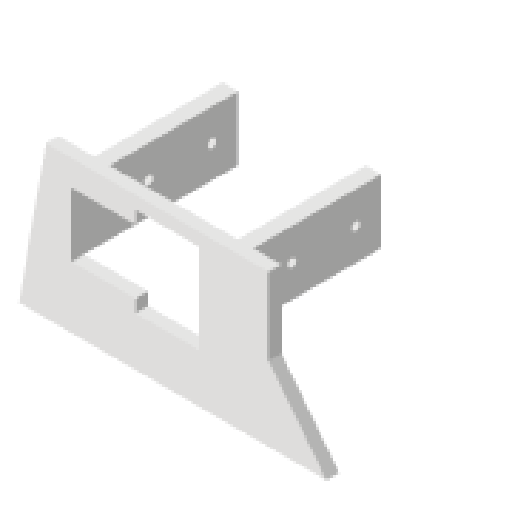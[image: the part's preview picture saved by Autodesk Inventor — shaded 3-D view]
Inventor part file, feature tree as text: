
AUTODESK INVENTOR PART (.ipt)
format: ipt  version: 2025.1 (Build 291241000, 241)  size: 164,352 bytes
history: native  units: mm
features: sketch x8, extrude x5, hole x3, other x1
ambient origin geometry x8: Origin, YZ Plane, XZ Plane, XY Plane, X Axis, Y Axis, Z Axis, Center Point
bodies: Body1 (feature_tree), Body2 (feature_tree)
feature tree (17):
  other  "Bryła1"
  extrude  "Wyciągnięcie proste1"  Depth=120.0mm
  extrude  "Wyciągnięcie proste2"  Depth=60.0mm
  extrude  "Wyciągnięcie proste3"  Depth=13.962634mm
  extrude  "Wyciągnięcie proste4"  Depth=60.0mm
  hole  "Otwór1"  [1 undecoded]
  hole  "Otwór2"  [1 undecoded]
  hole  "Otwór3"  [1 undecoded]
  extrude  "Wyciągnięcie proste7"  Depth=25.0mm
  sketch  "Szkic1"
  sketch  "Szkic2"
  sketch  "Szkic3"
  sketch  "Szkic4"
  sketch  "Szkic5"
  sketch  "Szkic7"
  sketch  "Szkic8"
  sketch  "Szkic10"
note: 3 required parameter values undecoded (feature->parameter linkage not recoverable at this tier; creation-order binding heuristic only, values carry confidence <= 0.55)
